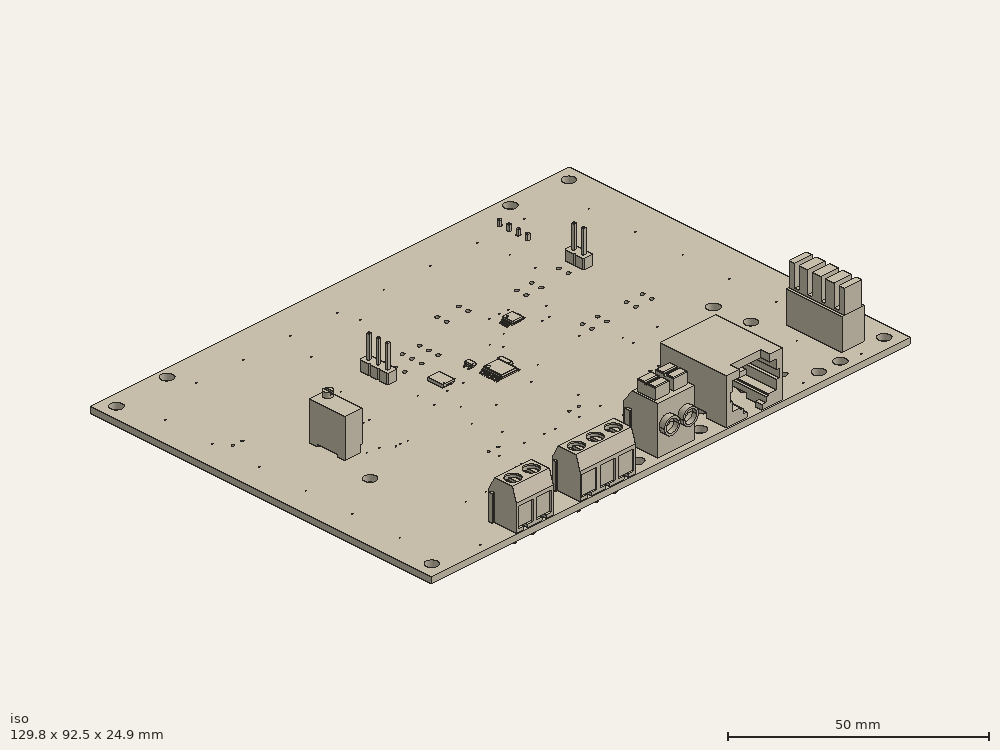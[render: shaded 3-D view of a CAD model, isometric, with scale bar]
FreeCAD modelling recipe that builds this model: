
FCSTD DOCUMENT  (FreeCAD 0.19R24276 (Git))
Label: pcb
License: All rights reserved
LicenseURL: http://en.wikipedia.org/wiki/All_rights_reserved
objects: App::Link×77, Part::Feature×49, App::Part×6, PartDesign::CoordinateSystem×1, Sketcher::SketchObject×1
note: 51 computed .brp shape members not serialized (recipe doc carries the construction recipe); baked Part::Feature solids carry a one-line shape summary decoded from their .brp

FEATURE [PartDesign::CoordinateSystem] Local_CS_d3e4
  AttacherType = Attacher::AttachEngine3D
FEATURE [Part::Feature] Pcb_d3e4
  Placement = pos=(-202.882,114.808,0) rot=(0,0,1;0rad)
  shape: bbox 129.8 x 92.46 x 1.6 mm, 180 faces (baked)
FEATURE [Sketcher::SketchObject] PCB_Sketch_d3e4
  FullyConstrained = false
  sketch-geometry (6):
    g0: LineSegment StartX=-64.77 StartY=-46.228 StartZ=0 EndX=-64.77 EndY=46.228 EndZ=0
    g1: LineSegment StartX=65.024 StartY=-46.228 StartZ=0 EndX=-64.77 EndY=-46.228 EndZ=0
    g2: LineSegment StartX=65.024 StartY=46.228 StartZ=0 EndX=65.024 EndY=-46.228 EndZ=0
    g3: LineSegment StartX=-64.77 StartY=46.228 StartZ=0 EndX=65.024 EndY=46.228 EndZ=0
    g4: Circle CenterX=49.0855 CenterY=-43.18 CenterZ=0 NormalX=0 NormalY=0 NormalZ=1 AngleXU=0 Radius=1.5
    g5: Circle CenterX=43.2435 CenterY=-43.18 CenterZ=0 NormalX=0 NormalY=0 NormalZ=1 AngleXU=0 Radius=1.5
  constraints (4):
    c: Coincident(g0,g1)
    c: Coincident(g0,g3)
    c: Coincident(g1,g2)
    c: Coincident(g2,g3)
FEATURE [Part::Feature] Shape  label="P1_PinSocket_1x04_P2.54mm_Vertical_2.5x8.4mm_621AF07D"
  Placement = pos=(39.6927,43.5983,-1.6) rot=(1,0,0;3.14159rad)
  shape: bbox 2.5 x 10.16 x 11.55 mm, 82 faces, 5 solids (baked)
FEATURE [Part::Feature] Shape001  label="D11_D_SOD_323_62342803"
  Placement = pos=(30.226,-25.4,0) rot=(0,0,1;0rad)
  shape: bbox 2.5 x 1.25 x 1.1 mm, 67 faces (baked)
FEATURE [Part::Feature] Shape002  label="R29_Gabarit - T93_2000000000.0"
  Placement = pos=(-42.7585,6.548,4.9) rot=(0,0,1;3.14159rad)
  shape: bbox 4.618 x 9.618 x 16.02 mm, 157 faces (baked)
FEATURE [Part::Feature] Part__Feature  label="BODY-TSSOP"
  Placement = pos=(0,0,0.68) rot=(1,0,0;1.5708rad)
  shape: bbox 4.402 x 5.002 x 1 mm, 74 faces (baked)
FEATURE [Part::Feature] Part__Feature001  label="LEAD-TSSOP"
  Placement = pos=(-2.575,2.275,0.25) rot=(0.57735,-0.57735,-0.57735;2.0944rad)
  shape: bbox 1 x 0.245 x 0.68 mm, 14 faces (baked)
FEATURE [Part::Feature] Part__Feature002  label="LEAD-TSSOP001"
  Placement = pos=(-2.575,1.625,0.25) rot=(0.57735,-0.57735,-0.57735;2.0944rad)
  shape: bbox 1 x 0.245 x 0.68 mm, 14 faces (baked)
FEATURE [Part::Feature] Part__Feature003  label="LEAD-TSSOP002"
  Placement = pos=(-2.575,0.975,0.25) rot=(0.57735,-0.57735,-0.57735;2.0944rad)
  shape: bbox 1 x 0.245 x 0.68 mm, 14 faces (baked)
FEATURE [Part::Feature] Part__Feature004  label="LEAD-TSSOP003"
  Placement = pos=(-2.575,0.325,0.25) rot=(0.57735,-0.57735,-0.57735;2.0944rad)
  shape: bbox 1 x 0.245 x 0.68 mm, 14 faces (baked)
FEATURE [Part::Feature] Part__Feature005  label="LEAD-TSSOP004"
  Placement = pos=(-2.575,-0.325,0.25) rot=(0.57735,-0.57735,-0.57735;2.0944rad)
  shape: bbox 1 x 0.245 x 0.68 mm, 14 faces (baked)
FEATURE [Part::Feature] Part__Feature006  label="LEAD-TSSOP005"
  Placement = pos=(-2.575,-0.975,0.25) rot=(0.57735,-0.57735,-0.57735;2.0944rad)
  shape: bbox 1 x 0.245 x 0.68 mm, 14 faces (baked)
FEATURE [Part::Feature] Part__Feature007  label="LEAD-TSSOP006"
  Placement = pos=(-2.575,-1.625,0.25) rot=(0.57735,-0.57735,-0.57735;2.0944rad)
  shape: bbox 1 x 0.245 x 0.68 mm, 14 faces (baked)
FEATURE [Part::Feature] Part__Feature008  label="LEAD-TSSOP007"
  Placement = pos=(-2.575,-2.275,0.25) rot=(0.57735,-0.57735,-0.57735;2.0944rad)
  shape: bbox 1 x 0.245 x 0.68 mm, 14 faces (baked)
FEATURE [Part::Feature] Part__Feature009  label="LEAD-TSSOP008"
  Placement = pos=(2.575,-2.275,0.25) rot=(0.57735,0.57735,0.57735;2.0944rad)
  shape: bbox 1 x 0.245 x 0.68 mm, 14 faces (baked)
FEATURE [Part::Feature] Part__Feature010  label="LEAD-TSSOP009"
  Placement = pos=(2.575,-1.625,0.25) rot=(0.57735,0.57735,0.57735;2.0944rad)
  shape: bbox 1 x 0.245 x 0.68 mm, 14 faces (baked)
FEATURE [Part::Feature] Part__Feature011  label="LEAD-TSSOP010"
  Placement = pos=(2.575,-0.975,0.25) rot=(0.57735,0.57735,0.57735;2.0944rad)
  shape: bbox 1 x 0.245 x 0.68 mm, 14 faces (baked)
FEATURE [Part::Feature] Part__Feature012  label="LEAD-TSSOP011"
  Placement = pos=(2.575,-0.325,0.25) rot=(0.57735,0.57735,0.57735;2.0944rad)
  shape: bbox 1 x 0.245 x 0.68 mm, 14 faces (baked)
FEATURE [Part::Feature] Part__Feature013  label="LEAD-TSSOP012"
  Placement = pos=(2.575,0.325,0.25) rot=(0.57735,0.57735,0.57735;2.0944rad)
  shape: bbox 1 x 0.245 x 0.68 mm, 14 faces (baked)
FEATURE [Part::Feature] Part__Feature014  label="LEAD-TSSOP013"
  Placement = pos=(2.575,0.975,0.25) rot=(0.57735,0.57735,0.57735;2.0944rad)
  shape: bbox 1 x 0.245 x 0.68 mm, 14 faces (baked)
FEATURE [Part::Feature] Part__Feature015  label="LEAD-TSSOP014"
  Placement = pos=(2.575,1.625,0.25) rot=(0.57735,0.57735,0.57735;2.0944rad)
  shape: bbox 1 x 0.245 x 0.68 mm, 14 faces (baked)
FEATURE [Part::Feature] Part__Feature016  label="LEAD-TSSOP015"
  Placement = pos=(2.575,2.275,0.25) rot=(0.57735,0.57735,0.57735;2.0944rad)
  shape: bbox 1 x 0.245 x 0.68 mm, 14 faces (baked)
FEATURE [Part::Feature] Part__Feature017  label="DAP"
  Placement = pos=(0,0,0.13) rot=(1,0,0;1.5708rad)
  shape: bbox 2.509 x 2.91 x 0.15 mm, 30 faces (baked)
FEATURE [App::Part] htssop_16_ASM  label="U4_htssop_16_ASM_621AF4F5"
  Group = -> [Part__Feature,Part__Feature001,Part__Feature002,Part__Feature003,Part__Feature004,Part__Feature005,Part__Feature006,Part__Feature007,Part__Feature008,Part__Feature009,Part__Feature010,Part__Feature011,Part__Feature012,Part__Feature013,Part__Feature014,Part__Feature015,Part__Feature016,Part__Feature017]
  Origin = -> Origin008
  Placement = pos=(-33.2105,-0.762,0) rot=(0,0,1;1.5708rad)
FEATURE [Part::Feature] Shape003  label="U1_TSSOP_10_3x3mm_P05mm_621AF491"
  Placement = pos=(15.5575,12.192,0) rot=(0,0,1;0rad)
  shape: bbox 4.9 x 3 x 1 mm, 186 faces (baked)
FEATURE [Part::Feature] Shape004  label="Q4_sot_323_621AF20D"
  Placement = pos=(-2.4765,5.588,0) rot=(0,0,-1;1.5708rad)
  shape: bbox 2.3 x 2.105 x 1.01 mm, 57 faces (baked)
FEATURE [Part::Feature] Shape005  label="U3_part_621AF4C8"
  Placement = pos=(-10.6045,5.334,0) rot=(0,0,1;1.5708rad)
  shape: bbox 3.098 x 4.09 x 0.8155 mm, 95 faces, 13 solids (baked)
FEATURE [Part::Feature] Shape006  label="R38_r_1206_62343314"
  Placement = pos=(27.178,-21.59,0) rot=(0,0,-1;1.5708rad)
  shape: bbox 1.6 x 3.2 x 0.55 mm, 26 faces (baked)
FEATURE [App::Link] R38_r_1206_62343314_ln_  label="R37_r_1206_62343301"
  LinkPlacement = pos=(23.114,-25.654,0) rot=(0,0,1;0rad)
  LinkedObject = -> Shape006
  Placement = pos=(23.114,-25.654,0) rot=(0,0,1;0rad)
FEATURE [Part::Feature] Shape007  label="Q6_SOT_23_62342DE3"
  Placement = pos=(30.48,-21.59,0) rot=(0,0,-1;1.5708rad)
  shape: bbox 3 x 2.5 x 1.2 mm, 76 faces (baked)
FEATURE [Part::Feature] Shape008  label="D22_smc_6234292A"
  Placement = pos=(-36.322,-37.084,-1.6) rot=(1,0,0;3.14159rad)
  shape: bbox 8 x 5.9 x 2.31 mm, 41 faces (baked)
FEATURE [Part::Feature] Shape009  label="D15_sod_523_6220D316"
  Placement = pos=(35.8775,-17.78,0) rot=(0,0.707107,0.707107;3.14159rad)
  shape: bbox 1.6 x 0.8066 x 0.7 mm, 39 faces (baked)
FEATURE [App::Link] D15_sod_523_6220D316_ln_  label="D14_sod_523_62342870"
  LinkPlacement = pos=(30.734,-18.288,0) rot=(1,0,0;1.5708rad)
  LinkedObject = -> Shape009
  Placement = pos=(30.734,-18.288,0) rot=(1,0,0;1.5708rad)
FEATURE [App::Link] D15_sod_523_6220D316_ln_001  label="D10_sod_523_6240D407"
  LinkPlacement = pos=(-11.6205,-29.464,-1.6) rot=(-1,0,0;1.5708rad)
  LinkedObject = -> Shape009
  Placement = pos=(-11.6205,-29.464,-1.6) rot=(-1,0,0;1.5708rad)
FEATURE [App::Link] D15_sod_523_6220D316_ln_002  label="D9_sod_523_621AEEC4"
  LinkPlacement = pos=(-17.2085,-29.464,-1.6) rot=(-1,0,0;1.5708rad)
  LinkedObject = -> Shape009
  Placement = pos=(-17.2085,-29.464,-1.6) rot=(-1,0,0;1.5708rad)
FEATURE [App::Link] D15_sod_523_6220D316_ln_003  label="D8_sod_523_621AEEAD"
  LinkPlacement = pos=(-22.7965,-29.464,-1.6) rot=(-1,0,0;1.5708rad)
  LinkedObject = -> Shape009
  Placement = pos=(-22.7965,-29.464,-1.6) rot=(-1,0,0;1.5708rad)
FEATURE [App::Link] D15_sod_523_6220D316_ln_004  label="D3_sod_523_6234F1D7"
  LinkPlacement = pos=(35.56,32.004,0) rot=(0,0.707107,0.707107;3.14159rad)
  LinkedObject = -> Shape009
  Placement = pos=(35.56,32.004,0) rot=(0,0.707107,0.707107;3.14159rad)
FEATURE [App::Link] D15_sod_523_6220D316_ln_005  label="D2_sod_523_6234F195"
  LinkPlacement = pos=(35.56,34.544,0) rot=(0,0.707107,0.707107;3.14159rad)
  LinkedObject = -> Shape009
  Placement = pos=(35.56,34.544,0) rot=(0,0.707107,0.707107;3.14159rad)
FEATURE [App::Link] D15_sod_523_6220D316_ln_006  label="D1_sod_523_62418C35"
  LinkPlacement = pos=(35.56,37.084,0) rot=(0,0.707107,0.707107;3.14159rad)
  LinkedObject = -> Shape009
  Placement = pos=(35.56,37.084,0) rot=(0,0.707107,0.707107;3.14159rad)
FEATURE [Part::Feature] Shape010  label="J4_pins_part_622DB727"
  Placement = pos=(54.61,-33.616,0) rot=(0,0,-1;1.5708rad)
  shape: bbox 6 x 15 x 17 mm, 48 faces (baked)
FEATURE [App::Link] J4_pins_part_622DB727_ln_  label="J1_pins_part_622DB76C"
  LinkPlacement = pos=(37.9095,-33.616,0) rot=(0,0,-1;1.5708rad)
  LinkedObject = -> Shape010
  Placement = pos=(37.9095,-33.616,0) rot=(0,0,-1;1.5708rad)
FEATURE [App::Link] R38_r_1206_62343314_ln_001  label="R11_r_1206_621AF2DE"
  LinkPlacement = pos=(32.0675,0.762,0) rot=(0,0,-1;1.5708rad)
  LinkedObject = -> Shape006
  Placement = pos=(32.0675,0.762,0) rot=(0,0,-1;1.5708rad)
FEATURE [Part::Feature] Shape011  label="D7_soic_8_6220D231"
  Placement = pos=(33.7185,-15.748,-1.6) rot=(0.707107,0.707107,0;3.14159rad)
  shape: bbox 4.9 x 6 x 1.7 mm, 125 faces (baked)
FEATURE [App::Link] R38_r_1206_62343314_ln_002  label="R35_r_1206_621CA02D"
  LinkPlacement = pos=(10.9855,-20.066,0) rot=(0,0,-1;1.5708rad)
  LinkedObject = -> Shape006
  Placement = pos=(10.9855,-20.066,0) rot=(0,0,-1;1.5708rad)
FEATURE [App::Link] R38_r_1206_62343314_ln_003  label="R34_r_1206_621CA01A"
  LinkPlacement = pos=(-10.8585,-20.066,0) rot=(0,0,-1;1.5708rad)
  LinkedObject = -> Shape006
  Placement = pos=(-10.8585,-20.066,0) rot=(0,0,-1;1.5708rad)
FEATURE [App::Link] R38_r_1206_62343314_ln_004  label="R33_r_1206_621CA007"
  LinkPlacement = pos=(-32.7025,-20.066,0) rot=(0,0,-1;1.5708rad)
  LinkedObject = -> Shape006
  Placement = pos=(-32.7025,-20.066,0) rot=(0,0,-1;1.5708rad)
FEATURE [Part::Feature] Shape012  label="L1_l_1206_621B00A5"
  Placement = pos=(5.6515,-36.068,-1.6) rot=(0.707107,0.707107,0;3.14159rad)
  shape: bbox 1.6 x 3.2 x 1.6 mm, 28 faces (baked)
FEATURE [Part::Feature] Shape013  label="U2_sot_23_3_621AF4A7"
  Placement = pos=(2.8575,1.524,0.3) rot=(0.57735,0.57735,0.57735;2.0944rad)
  shape: bbox 2.476 x 2.92 x 1.02 mm, 73 faces (baked)
FEATURE [App::Link] R38_r_1206_62343314_ln_005  label="R32_r_1206_621AF473"
  LinkPlacement = pos=(-54.864,19.05,0) rot=(0,0,1;0rad)
  LinkedObject = -> Shape006
  Placement = pos=(-54.864,19.05,0) rot=(0,0,1;0rad)
FEATURE [App::Link] R38_r_1206_62343314_ln_006  label="R31_r_1206_621AF460"
  LinkPlacement = pos=(-2.7305,1.778,0) rot=(0,0,1;3.14159rad)
  LinkedObject = -> Shape006
  Placement = pos=(-2.7305,1.778,0) rot=(0,0,1;3.14159rad)
FEATURE [App::Link] R38_r_1206_62343314_ln_007  label="R30_r_1206_621AF44D"
  LinkPlacement = pos=(-42.6085,8.636,0) rot=(0,0,1;3.14159rad)
  LinkedObject = -> Shape006
  Placement = pos=(-42.6085,8.636,0) rot=(0,0,1;3.14159rad)
FEATURE [App::Link] R38_r_1206_62343314_ln_008  label="R28_r_1206_621AF421"
  LinkPlacement = pos=(-5.7785,5.588,0) rot=(0,0,-1;1.5708rad)
  LinkedObject = -> Shape006
  Placement = pos=(-5.7785,5.588,0) rot=(0,0,-1;1.5708rad)
FEATURE [App::Link] R38_r_1206_62343314_ln_009  label="R27_r_1206_621AF40E"
  LinkPlacement = pos=(1.0795,16.764,0) rot=(0,0,1;1.5708rad)
  LinkedObject = -> Shape006
  Placement = pos=(1.0795,16.764,0) rot=(0,0,1;1.5708rad)
FEATURE [App::Link] R38_r_1206_62343314_ln_010  label="R26_r_1206_623FABCB"
  LinkPlacement = pos=(-30.6705,0.762,-1.6) rot=(0,1,0;3.14159rad)
  LinkedObject = -> Shape006
  Placement = pos=(-30.6705,0.762,-1.6) rot=(0,1,0;3.14159rad)
FEATURE [App::Link] R38_r_1206_62343314_ln_011  label="R25_r_1206_621AF3E8"
  LinkPlacement = pos=(-30.6705,-2.032,-1.6) rot=(1,0,0;3.14159rad)
  LinkedObject = -> Shape006
  Placement = pos=(-30.6705,-2.032,-1.6) rot=(1,0,0;3.14159rad)
FEATURE [App::Link] R38_r_1206_62343314_ln_012  label="R24_r_1206_621AF3D5"
  LinkPlacement = pos=(-35.7505,0.762,-1.6) rot=(1,0,0;3.14159rad)
  LinkedObject = -> Shape006
  Placement = pos=(-35.7505,0.762,-1.6) rot=(1,0,0;3.14159rad)
FEATURE [App::Link] R38_r_1206_62343314_ln_013  label="R23_r_1206_621AF3C2"
  LinkPlacement = pos=(-35.7505,-2.032,-1.6) rot=(1,0,0;3.14159rad)
  LinkedObject = -> Shape006
  Placement = pos=(-35.7505,-2.032,-1.6) rot=(1,0,0;3.14159rad)
FEATURE [App::Link] R38_r_1206_62343314_ln_014  label="R22_r_1206_621AF3AF"
  LinkPlacement = pos=(21.9075,-16.764,0) rot=(0,0,1;0rad)
  LinkedObject = -> Shape006
  Placement = pos=(21.9075,-16.764,0) rot=(0,0,1;0rad)
FEATURE [App::Link] R38_r_1206_62343314_ln_015  label="R21_r_1206_621AF39C"
  LinkPlacement = pos=(14.0335,-20.066,0) rot=(0,0,-1;1.5708rad)
  LinkedObject = -> Shape006
  Placement = pos=(14.0335,-20.066,0) rot=(0,0,-1;1.5708rad)
FEATURE [App::Link] R38_r_1206_62343314_ln_016  label="R20_r_1206_621AF389"
  LinkPlacement = pos=(36.1315,24.638,0) rot=(0,0,-1;1.5708rad)
  LinkedObject = -> Shape006
  Placement = pos=(36.1315,24.638,0) rot=(0,0,-1;1.5708rad)
FEATURE [App::Link] R38_r_1206_62343314_ln_017  label="R19_r_1206_621AF376"
  LinkPlacement = pos=(40.1955,24.638,0) rot=(0,0,1;1.5708rad)
  LinkedObject = -> Shape006
  Placement = pos=(40.1955,24.638,0) rot=(0,0,1;1.5708rad)
FEATURE [App::Link] R38_r_1206_62343314_ln_018  label="R18_r_1206_621AF363"
  LinkPlacement = pos=(32.3215,18.542,0) rot=(0,0,-1;1.5708rad)
  LinkedObject = -> Shape006
  Placement = pos=(32.3215,18.542,0) rot=(0,0,-1;1.5708rad)
FEATURE [App::Link] R38_r_1206_62343314_ln_019  label="R17_r_1206_621AF350"
  LinkPlacement = pos=(24.4475,24.638,0) rot=(0,0,-1;1.5708rad)
  LinkedObject = -> Shape006
  Placement = pos=(24.4475,24.638,0) rot=(0,0,-1;1.5708rad)
FEATURE [App::Link] R38_r_1206_62343314_ln_020  label="R16_r_1206_621AF33D"
  LinkPlacement = pos=(28.7655,24.638,0) rot=(0,0,-1;1.5708rad)
  LinkedObject = -> Shape006
  Placement = pos=(28.7655,24.638,0) rot=(0,0,-1;1.5708rad)
FEATURE [App::Link] R38_r_1206_62343314_ln_021  label="R15_r_1206_621AF32A"
  LinkPlacement = pos=(0.0635,-16.764,0) rot=(0,0,1;0rad)
  LinkedObject = -> Shape006
  Placement = pos=(0.0635,-16.764,0) rot=(0,0,1;0rad)
FEATURE [App::Link] R38_r_1206_62343314_ln_022  label="R14_r_1206_621AF317"
  LinkPlacement = pos=(-7.8105,-20.066,0) rot=(0,0,-1;1.5708rad)
  LinkedObject = -> Shape006
  Placement = pos=(-7.8105,-20.066,0) rot=(0,0,-1;1.5708rad)
FEATURE [App::Link] R38_r_1206_62343314_ln_023  label="R13_r_1206_621BB122"
  LinkPlacement = pos=(24.1935,6.604,0) rot=(0,0,-1;1.5708rad)
  LinkedObject = -> Shape006
  Placement = pos=(24.1935,6.604,0) rot=(0,0,-1;1.5708rad)
FEATURE [App::Link] R38_r_1206_62343314_ln_024  label="R12_r_1206_621AF2F1"
  LinkPlacement = pos=(28.2575,6.604,0) rot=(0,0,1;1.5708rad)
  LinkedObject = -> Shape006
  Placement = pos=(28.2575,6.604,0) rot=(0,0,1;1.5708rad)
FEATURE [App::Link] R38_r_1206_62343314_ln_025  label="R10_r_1206_621AF2CB"
  LinkPlacement = pos=(36.3855,6.35,0) rot=(0,0,-1;1.5708rad)
  LinkedObject = -> Shape006
  Placement = pos=(36.3855,6.35,0) rot=(0,0,-1;1.5708rad)
FEATURE [App::Link] R38_r_1206_62343314_ln_026  label="R9_r_1206_621AF2B8"
  LinkPlacement = pos=(40.4495,6.35,0) rot=(0,0,-1;1.5708rad)
  LinkedObject = -> Shape006
  Placement = pos=(40.4495,6.35,0) rot=(0,0,-1;1.5708rad)
FEATURE [App::Link] R38_r_1206_62343314_ln_027  label="R8_r_1206_621AF2A5"
  LinkPlacement = pos=(-21.7805,-16.764,0) rot=(0,0,1;0rad)
  LinkedObject = -> Shape006
  Placement = pos=(-21.7805,-16.764,0) rot=(0,0,1;0rad)
FEATURE [App::Link] R38_r_1206_62343314_ln_028  label="R7_r_1206_621AF292"
  LinkPlacement = pos=(-29.6545,-20.066,0) rot=(0,0,-1;1.5708rad)
  LinkedObject = -> Shape006
  Placement = pos=(-29.6545,-20.066,0) rot=(0,0,-1;1.5708rad)
FEATURE [App::Link] R38_r_1206_62343314_ln_029  label="R6_r_1206_621AF27F"
  LinkPlacement = pos=(12.2555,27.94,0) rot=(0,0,-1;1.5708rad)
  LinkedObject = -> Shape006
  Placement = pos=(12.2555,27.94,0) rot=(0,0,-1;1.5708rad)
FEATURE [App::Link] R38_r_1206_62343314_ln_030  label="R5_r_1206_6220FDA9"
  LinkPlacement = pos=(6.4135,27.94,0) rot=(0,0,-1;1.5708rad)
  LinkedObject = -> Shape006
  Placement = pos=(6.4135,27.94,0) rot=(0,0,-1;1.5708rad)
FEATURE [App::Link] R38_r_1206_62343314_ln_031  label="R4_r_1206_6220D3EA"
  LinkPlacement = pos=(28.702,-23.622,-1.6) rot=(0.707107,0.707107,0;3.14159rad)
  LinkedObject = -> Shape006
  Placement = pos=(28.702,-23.622,-1.6) rot=(0.707107,0.707107,0;3.14159rad)
FEATURE [App::Link] R38_r_1206_62343314_ln_032  label="R3_r_1206_6220D420"
  LinkPlacement = pos=(31.6865,-23.622,-1.6) rot=(0.707107,0.707107,0;3.14159rad)
  LinkedObject = -> Shape006
  Placement = pos=(31.6865,-23.622,-1.6) rot=(0.707107,0.707107,0;3.14159rad)
FEATURE [App::Link] R38_r_1206_62343314_ln_033  label="R2_r_1206_6220D456"
  LinkPlacement = pos=(38.862,-23.622,-1.6) rot=(0.707107,0.707107,0;3.14159rad)
  LinkedObject = -> Shape006
  Placement = pos=(38.862,-23.622,-1.6) rot=(0.707107,0.707107,0;3.14159rad)
FEATURE [App::Link] R38_r_1206_62343314_ln_034  label="R1_r_1206_6220D5BE"
  LinkPlacement = pos=(35.7505,-23.622,-1.6) rot=(0.707107,0.707107,0;3.14159rad)
  LinkedObject = -> Shape006
  Placement = pos=(35.7505,-23.622,-1.6) rot=(0.707107,0.707107,0;3.14159rad)
FEATURE [App::Link] Q4_sot_323_621AF20D_ln_  label="Q3_sot_323_621AF1F7"
  LinkPlacement = pos=(17.3355,-20.066,0) rot=(0,0,-1;1.5708rad)
  LinkedObject = -> Shape004
  Placement = pos=(17.3355,-20.066,0) rot=(0,0,-1;1.5708rad)
FEATURE [App::Link] Q4_sot_323_621AF20D_ln_001  label="Q2_sot_323_621AF1E1"
  LinkPlacement = pos=(-4.5085,-20.066,0) rot=(0,0,-1;1.5708rad)
  LinkedObject = -> Shape004
  Placement = pos=(-4.5085,-20.066,0) rot=(0,0,-1;1.5708rad)
FEATURE [App::Link] Q4_sot_323_621AF20D_ln_002  label="Q1_sot_323_621AF1CB"
  LinkPlacement = pos=(-26.3525,-20.066,0) rot=(0,0,-1;1.5708rad)
  LinkedObject = -> Shape004
  Placement = pos=(-26.3525,-20.066,0) rot=(0,0,-1;1.5708rad)
FEATURE [Part::Feature] Shape014  label="P15_PinHeader_1x03_P254mm_Vertical_621AF1B5"
  Placement = pos=(-17.4625,12.954,0) rot=(0,0,1;3.14159rad)
  shape: bbox 2.54 x 7.62 x 11.54 mm, 76 faces (baked)
FEATURE [App::Link] P15_PinHeader_1x03_P254mm_Vertical_621AF1B5_ln_  label="P14_PinHeader_1x03_P254mm_Vertical_621AF19E"
  LinkPlacement = pos=(-12.8905,12.954,0) rot=(0,0,1;3.14159rad)
  LinkedObject = -> Shape014
  Placement = pos=(-12.8905,12.954,0) rot=(0,0,1;3.14159rad)
FEATURE [App::Link] P15_PinHeader_1x03_P254mm_Vertical_621AF1B5_ln_001  label="P13_PinHeader_1x03_P254mm_Vertical_621AF187"
  LinkPlacement = pos=(-8.3185,12.954,0) rot=(0,0,1;3.14159rad)
  LinkedObject = -> Shape014
  Placement = pos=(-8.3185,12.954,0) rot=(0,0,1;3.14159rad)
FEATURE [App::Link] P15_PinHeader_1x03_P254mm_Vertical_621AF1B5_ln_002  label="P12_PinHeader_1x03_P254mm_Vertical_621AF170"
  LinkPlacement = pos=(-3.7465,12.954,0) rot=(0,0,1;3.14159rad)
  LinkedObject = -> Shape014
  Placement = pos=(-3.7465,12.954,0) rot=(0,0,1;3.14159rad)
FEATURE [Part::Feature] Shape015  label="P11_PinHeader_1x02_P254mm_Vertical_621AF159"
  Placement = pos=(40.1955,20.066,0) rot=(0,0,1;0rad)
  shape: bbox 2.54 x 5.08 x 11.54 mm, 52 faces (baked)
FEATURE [App::Link] P11_PinHeader_1x02_P254mm_Vertical_621AF159_ln_  label="P10_PinHeader_1x02_P254mm_Vertical_621AF143"
  LinkPlacement = pos=(36.1315,17.526,0) rot=(0,0,1;3.14159rad)
  LinkedObject = -> Shape015
  Placement = pos=(36.1315,17.526,0) rot=(0,0,1;3.14159rad)
FEATURE [App::Link] P11_PinHeader_1x02_P254mm_Vertical_621AF159_ln_001  label="P9_PinHeader_1x02_P254mm_Vertical_621AF12D"
  LinkPlacement = pos=(28.5115,19.812,0) rot=(0,0,1;0rad)
  LinkedObject = -> Shape015
  Placement = pos=(28.5115,19.812,0) rot=(0,0,1;0rad)
FEATURE [App::Link] P11_PinHeader_1x02_P254mm_Vertical_621AF159_ln_002  label="P8_PinHeader_1x02_P254mm_Vertical_621AF117"
  LinkPlacement = pos=(24.4475,17.272,0) rot=(0,0,1;3.14159rad)
  LinkedObject = -> Shape015
  Placement = pos=(24.4475,17.272,0) rot=(0,0,1;3.14159rad)
FEATURE [App::Link] P11_PinHeader_1x02_P254mm_Vertical_621AF159_ln_003  label="P7_PinHeader_1x02_P254mm_Vertical_621AF101"
  LinkPlacement = pos=(24.1935,1.778,0) rot=(0,0,1;0rad)
  LinkedObject = -> Shape015
  Placement = pos=(24.1935,1.778,0) rot=(0,0,1;0rad)
FEATURE [App::Link] P11_PinHeader_1x02_P254mm_Vertical_621AF159_ln_004  label="P6_PinHeader_1x02_P254mm_Vertical_621AF0EB"
  LinkPlacement = pos=(28.2575,-0.762,0) rot=(0,0,1;3.14159rad)
  LinkedObject = -> Shape015
  Placement = pos=(28.2575,-0.762,0) rot=(0,0,1;3.14159rad)
FEATURE [App::Link] P11_PinHeader_1x02_P254mm_Vertical_621AF159_ln_005  label="P5_PinHeader_1x02_P254mm_Vertical_621AF0D5"
  LinkPlacement = pos=(36.1315,1.778,0) rot=(0,0,1;0rad)
  LinkedObject = -> Shape015
  Placement = pos=(36.1315,1.778,0) rot=(0,0,1;0rad)
FEATURE [App::Link] P11_PinHeader_1x02_P254mm_Vertical_621AF159_ln_006  label="P4_PinHeader_1x02_P254mm_Vertical_621AF0BF"
  LinkPlacement = pos=(40.4495,-0.762,0) rot=(0,0,1;3.14159rad)
  LinkedObject = -> Shape015
  Placement = pos=(40.4495,-0.762,0) rot=(0,0,1;3.14159rad)
FEATURE [App::Link] P11_PinHeader_1x02_P254mm_Vertical_621AF159_ln_007  label="P3_PinHeader_1x02_P254mm_Vertical_621AF0A9"
  LinkPlacement = pos=(12.2555,20.828,0) rot=(0,0,1;3.14159rad)
  LinkedObject = -> Shape015
  Placement = pos=(12.2555,20.828,0) rot=(0,0,1;3.14159rad)
FEATURE [App::Link] P11_PinHeader_1x02_P254mm_Vertical_621AF159_ln_008  label="P2_PinHeader_1x02_P254mm_Vertical_6220FD6D"
  LinkPlacement = pos=(6.4135,20.828,0) rot=(0,0,1;3.14159rad)
  LinkedObject = -> Shape015
  Placement = pos=(6.4135,20.828,0) rot=(0,0,1;3.14159rad)
FEATURE [App::Link] L1_l_1206_621B00A5_ln_  label="L2_l_1206_621AF065"
  LinkPlacement = pos=(0.5715,-36.068,-1.6) rot=(0.707107,0.707107,0;3.14159rad)
  LinkedObject = -> Shape012
  Placement = pos=(0.5715,-36.068,-1.6) rot=(0.707107,0.707107,0;3.14159rad)
FEATURE [Part::Feature] Shape016  label="J6_FOB0BCC4F41wx7y_621AF03F"
  Placement = pos=(-56.4825,-45.926,-0.5) rot=(1,0,0;1.5708rad)
  shape: bbox 12.75 x 8.095 x 17.94 mm, 416 faces (baked)
FEATURE [Part::Feature] Shape017  label="J5_PRT0007_621AF02A"
  Placement = pos=(5.5175,-40.14,6) rot=(0,0.707107,0.707107;3.14159rad)
  shape: bbox 10.6 x 10.65 x 19.8 mm, 90 faces (baked)
FEATURE [Part::Feature] Shape018  label="J3_54601-908WPLF_6220D097"
  Placement = pos=(23.1775,-45.846,11.5) rot=(1,0,0;3.14159rad)
  shape: bbox 15.24 x 18 x 15.25 mm, 132 faces (baked)
FEATURE [Part::Feature] Shape019  label="J2_FOB0BCC4F41wxct_621AEFE1"
  Placement = pos=(-24.2325,-45.926,-0.5) rot=(1,0,0;1.5708rad)
  shape: bbox 30.92 x 30.92 x 17.94 mm, 452 faces (baked)
FEATURE [App::Link] Q6_SOT_23_62342DE3_ln_  label="D17_SOT_23_621AEF79"
  LinkPlacement = pos=(3.1115,-31.496,-1.6) rot=(0.707107,0.707107,0;3.14159rad)
  LinkedObject = -> Shape007
  Placement = pos=(3.1115,-31.496,-1.6) rot=(0.707107,0.707107,0;3.14159rad)
FEATURE [Part::Feature] Shape020  label="D12_part_6220D35D"
  Placement = pos=(35.3695,-22.098,0) rot=(0,0,-1;1.5708rad)
  shape: bbox 3.99 x 4.448 x 1.503 mm, 89 faces, 8 solids (baked)
FEATURE [App::Link] D12_part_6220D35D_ln_  label="D6_part_6240D3BB"
  LinkPlacement = pos=(-11.1125,-34.036,-1.6) rot=(-0.707107,0.707107,0;3.14159rad)
  LinkedObject = -> Shape020
  Placement = pos=(-11.1125,-34.036,-1.6) rot=(-0.707107,0.707107,0;3.14159rad)
FEATURE [App::Link] D12_part_6220D35D_ln_001  label="D5_part_621AEE5B"
  LinkPlacement = pos=(-16.7005,-34.036,-1.6) rot=(-0.707107,0.707107,0;3.14159rad)
  LinkedObject = -> Shape020
  Placement = pos=(-16.7005,-34.036,-1.6) rot=(-0.707107,0.707107,0;3.14159rad)
FEATURE [App::Link] D12_part_6220D35D_ln_002  label="D4_part_621AEE3F"
  LinkPlacement = pos=(-22.2885,-34.036,-1.6) rot=(-0.707107,0.707107,0;3.14159rad)
  LinkedObject = -> Shape020
  Placement = pos=(-22.2885,-34.036,-1.6) rot=(-0.707107,0.707107,0;3.14159rad)
FEATURE [Part::Feature] Shape021  label="C15_c_1206_621AEDDE"
  Placement = pos=(-35.4965,7.112,0) rot=(0,0,1;0rad)
  shape: bbox 3.2 x 1.6 x 1.6 mm, 28 faces (baked)
FEATURE [App::Link] C15_c_1206_621AEDDE_ln_  label="C14_c_1206_621AEDCB"
  LinkPlacement = pos=(-30.6705,7.112,0) rot=(0,0,1;0rad)
  LinkedObject = -> Shape021
  Placement = pos=(-30.6705,7.112,0) rot=(0,0,1;0rad)
FEATURE [App::Link] C15_c_1206_621AEDDE_ln_001  label="C13_c_1206_621AEDB8"
  LinkPlacement = pos=(-33.2105,-9.144,0) rot=(0,0,1;0rad)
  LinkedObject = -> Shape021
  Placement = pos=(-33.2105,-9.144,0) rot=(0,0,1;0rad)
FEATURE [App::Link] C15_c_1206_621AEDDE_ln_002  label="C12_c_1206_621AEDA5"
  LinkPlacement = pos=(2.8575,7.874,0) rot=(0,0,1;0rad)
  LinkedObject = -> Shape021
  Placement = pos=(2.8575,7.874,0) rot=(0,0,1;0rad)
FEATURE [App::Link] C15_c_1206_621AEDDE_ln_003  label="C11_c_1206_621AED92"
  LinkPlacement = pos=(2.8575,5.08,0) rot=(0,0,1;0rad)
  LinkedObject = -> Shape021
  Placement = pos=(2.8575,5.08,0) rot=(0,0,1;0rad)
FEATURE [App::Link] C15_c_1206_621AEDDE_ln_004  label="C10_c_1206_621AED7F"
  LinkPlacement = pos=(-10.6045,3.81,-1.6) rot=(0,1,0;3.14159rad)
  LinkedObject = -> Shape021
  Placement = pos=(-10.6045,3.81,-1.6) rot=(0,1,0;3.14159rad)
FEATURE [App::Link] C15_c_1206_621AEDDE_ln_005  label="C9_c_1206_621AED6C"
  LinkPlacement = pos=(-10.6045,-2.54,0) rot=(0,0,1;3.14159rad)
  LinkedObject = -> Shape021
  Placement = pos=(-10.6045,-2.54,0) rot=(0,0,1;3.14159rad)
FEATURE [App::Link] C15_c_1206_621AEDDE_ln_006  label="C8_c_1206_621AED59"
  LinkPlacement = pos=(-10.6045,0.254,0) rot=(0,0,1;0rad)
  LinkedObject = -> Shape021
  Placement = pos=(-10.6045,0.254,0) rot=(0,0,1;0rad)
FEATURE [App::Link] C15_c_1206_621AEDDE_ln_007  label="C7_c_1206_621AED46"
  LinkPlacement = pos=(-14.6685,-1.27,0) rot=(0,0,1;1.5708rad)
  LinkedObject = -> Shape021
  Placement = pos=(-14.6685,-1.27,0) rot=(0,0,1;1.5708rad)
FEATURE [App::Link] C15_c_1206_621AEDDE_ln_008  label="C6_c_1206_621AED33"
  LinkPlacement = pos=(2.8575,-1.778,0) rot=(0,0,1;0rad)
  LinkedObject = -> Shape021
  Placement = pos=(2.8575,-1.778,0) rot=(0,0,1;0rad)
FEATURE [App::Link] C15_c_1206_621AEDDE_ln_009  label="C5_c_1206_621AED20"
  LinkPlacement = pos=(2.8575,-4.572,0) rot=(0,0,1;0rad)
  LinkedObject = -> Shape021
  Placement = pos=(2.8575,-4.572,0) rot=(0,0,1;0rad)
FEATURE [App::Part] Top_d3e4
  Group = -> [Shape001,Shape002,htssop_16_ASM,Shape003,Shape004,Shape005,Shape006,R38_r_1206_62343314_ln_,Shape007,Shape009,D15_sod_523_6220D316_ln_,D15_sod_523_6220D316_ln_004,D15_sod_523_6220D316_ln_005,D15_sod_523_6220D316_ln_006,Shape010,J4_pins_part_622DB727_ln_,R38_r_1206_62343314_ln_001,R38_r_1206_62343314_ln_002,R38_r_1206_62343314_ln_003,R38_r_1206_62343314_ln_004,Shape013,R38_r_1206_62343314_ln_005,+53 more]
  Origin = -> Origin003
FEATURE [App::Link] C15_c_1206_621AEDDE_ln_010  label="C4_c_1206_621AED0D"
  LinkPlacement = pos=(21.3995,12.954,-1.6) rot=(-0.707107,0.707107,0;3.14159rad)
  LinkedObject = -> Shape021
  Placement = pos=(21.3995,12.954,-1.6) rot=(-0.707107,0.707107,0;3.14159rad)
FEATURE [App::Link] C15_c_1206_621AEDDE_ln_011  label="C3_c_1206_621AECFA"
  LinkPlacement = pos=(18.6055,12.954,-1.6) rot=(-0.707107,0.707107,0;3.14159rad)
  LinkedObject = -> Shape021
  Placement = pos=(18.6055,12.954,-1.6) rot=(-0.707107,0.707107,0;3.14159rad)
FEATURE [App::Link] C15_c_1206_621AEDDE_ln_012  label="C2_c_1206_621AECE7"
  LinkPlacement = pos=(9.7155,12.954,-1.6) rot=(-0.707107,0.707107,0;3.14159rad)
  LinkedObject = -> Shape021
  Placement = pos=(9.7155,12.954,-1.6) rot=(-0.707107,0.707107,0;3.14159rad)
FEATURE [App::Link] C15_c_1206_621AEDDE_ln_013  label="C1_c_1206_621AECD4"
  LinkPlacement = pos=(12.5095,12.954,-1.6) rot=(-0.707107,0.707107,0;3.14159rad)
  LinkedObject = -> Shape021
  Placement = pos=(12.5095,12.954,-1.6) rot=(-0.707107,0.707107,0;3.14159rad)
FEATURE [App::Part] Bot_d3e4
  Group = -> [Shape,Shape008,D15_sod_523_6220D316_ln_001,D15_sod_523_6220D316_ln_002,D15_sod_523_6220D316_ln_003,Shape011,Shape012,R38_r_1206_62343314_ln_010,R38_r_1206_62343314_ln_011,R38_r_1206_62343314_ln_012,R38_r_1206_62343314_ln_013,R38_r_1206_62343314_ln_031,R38_r_1206_62343314_ln_032,R38_r_1206_62343314_ln_033,R38_r_1206_62343314_ln_034,L1_l_1206_621B00A5_ln_,Q6_SOT_23_62342DE3_ln_,+8 more]
  Origin = -> Origin004
FEATURE [App::Part] Step_Models_d3e4
  Group = -> [Top_d3e4,Bot_d3e4]
  Origin = -> Origin002
FEATURE [Part::Feature] pads_area180001  label="topPads_d3e4"
  Placement = pos=(-202.882,114.808,0.02) rot=(0,0,1;0rad)
  shape: bbox 128.7 x 91.95 x 2e-07 mm, 320 faces, 0 solids (baked)
FEATURE [Part::Feature] tracks_area001  label="topTracks_d3e4"
  Placement = pos=(-202.882,114.808,0.01) rot=(0,0,1;0rad)
  shape: bbox 110.3 x 82.63 x 2e-07 mm, 162 faces, 0 solids (baked)
FEATURE [Part::Feature] zones_area001  label="topZones_d3e4"
  Placement = pos=(-202.882,114.808,0.01) rot=(0,0,1;0rad)
  shape: bbox 128.7 x 91.39 x 2e-07 mm, 13 faces, 0 solids (baked)
FEATURE [Part::Feature] pads_area180152001  label="botPads_d3e4"
  Placement = pos=(-202.882,114.808,-1.62) rot=(0,0,1;0rad)
  shape: bbox 128.7 x 91.95 x 2e-07 mm, 237 faces, 0 solids (baked)
FEATURE [Part::Feature] tracks_area002001  label="botTracks_d3e4"
  Placement = pos=(-202.882,114.808,-1.61) rot=(0,0,1;0rad)
  shape: bbox 93.3 x 77.84 x 2e-07 mm, 55 faces, 0 solids (baked)
FEATURE [Part::Feature] zones_area002001  label="botZones_d3e4"
  Placement = pos=(-202.882,114.808,-1.61) rot=(0,0,1;0rad)
  shape: bbox 128.7 x 91.39 x 2e-07 mm, 6 faces, 0 solids (baked)
FEATURE [Part::Feature] botSilks_28
  Placement = pos=(-202.882,114.808,-1.67) rot=(0,0,1;0rad)
  shape: bbox 98.61 x 81.59 x 2e-07 mm, 112 faces, 0 solids (baked)
FEATURE [Part::Feature] topSilks_c1ee
  Placement = pos=(-202.882,114.808,0.07) rot=(0,0,1;0rad)
  shape: bbox 120.2 x 90.7 x 2e-07 mm, 493 faces, 0 solids (baked)
FEATURE [App::Part] Board_Geoms_d3e4
  Group = -> [Local_CS_d3e4,Pcb_d3e4,pads_area180001,tracks_area001,zones_area001,pads_area180152001,tracks_area002001,zones_area002001,botSilks_28,topSilks_c1ee,PCB_Sketch_d3e4]
  Origin = -> Origin
FEATURE [App::Part] Board_d3e4  label="signalization-by-fireplace"
  Group = -> [Board_Geoms_d3e4,Step_Models_d3e4]
  Origin = -> Origin001
